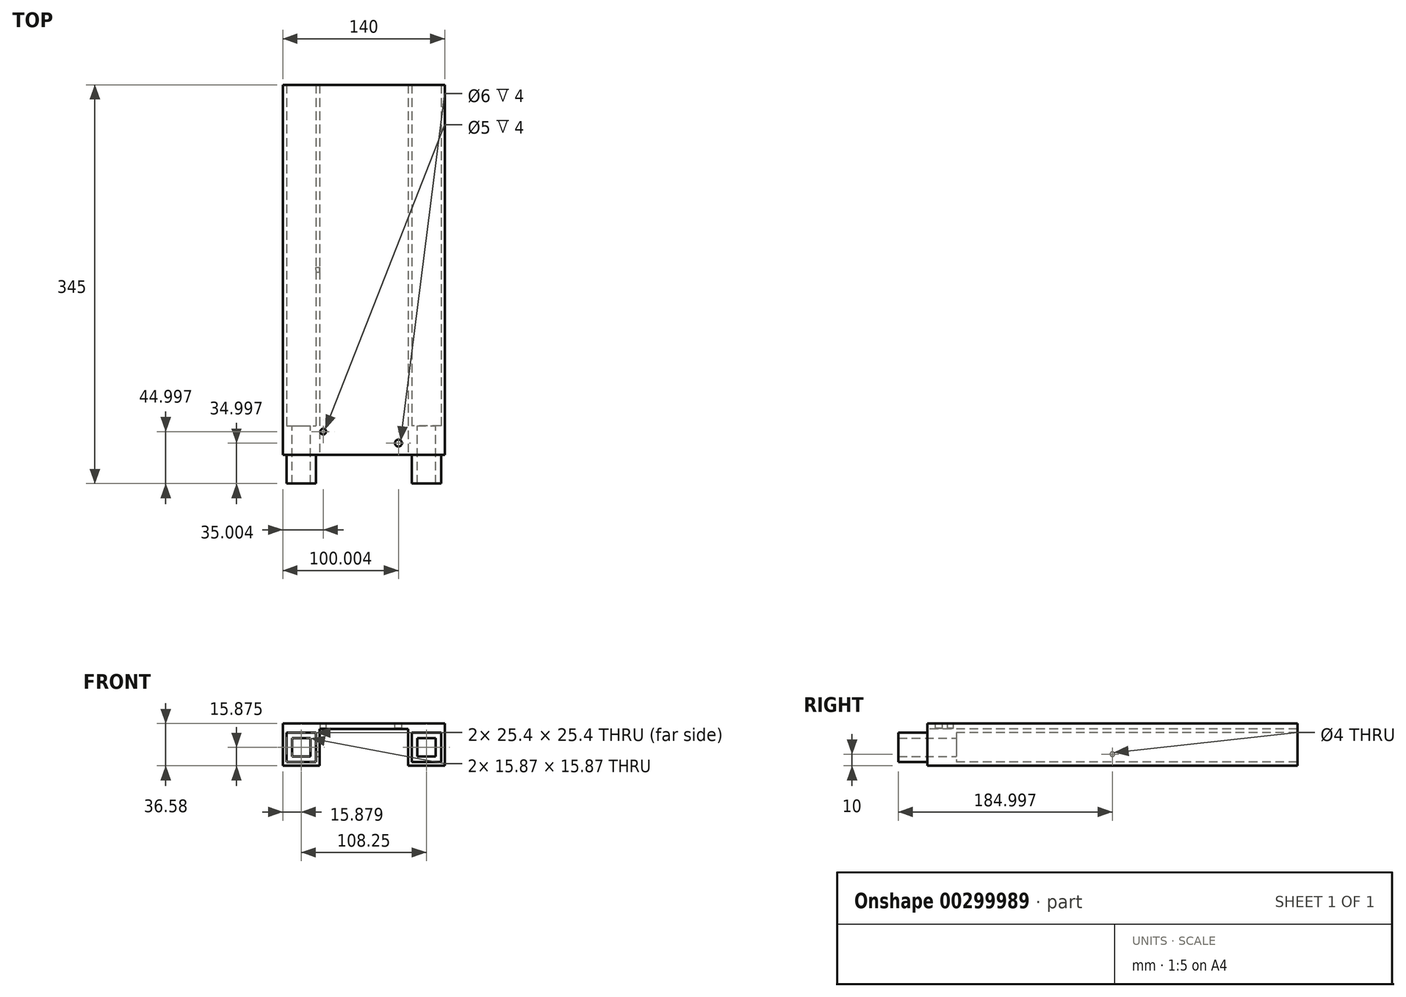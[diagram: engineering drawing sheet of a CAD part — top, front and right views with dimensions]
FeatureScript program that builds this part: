
annotation { "Feature Type Name" : "Feature", "Feature Type Description" : "" }
export const myFeature = defineFeature(function(context is Context, id is Id, definition is map)
    precondition{}
    {
        {
            var Q0;
            Q0=qCreatedBy(makeId("Top.planeOp"),FACE);
            var sketch = newSketch(context, id + "F0", { "sketchPlane" : qUnion([Q0])});
            skLineSegment(sketch, "E0.bottom", {"start": v(-71.28, 277.03) * mm, "end": v(68.72, 277.03) * mm});
            skLineSegment(sketch, "E0.top", {"start": v(-71.28, -42.97) * mm, "end": v(68.72, -42.97) * mm});
            skLineSegment(sketch, "E0.left", {"start": v(-71.28, 277.03) * mm, "end": v(-71.28, -42.97) * mm});
            skLineSegment(sketch, "E0.right", {"start": v(68.72, 277.03) * mm, "end": v(68.72, -42.97) * mm});
            skSolve(sketch);
        }
        {
            var Q0;
            Q0=makeQuery(id+"F0.imprint","IMPRINT",FACE,{"disambiguationData":[TD([[makeQuery(id+"F0.imprint","IMPRINT",EDGE,{"derivedFrom":sQuery(id+"F0.wireOp",EDGE,"E0.bottom")}),-1.0]])]});
            extrude(context, id + "F1", {"entities" : qUnion([Q0]), "depth" : 4.83 * mm, "offsetDistance" : 25 * mm});
        }
        {
            var Q0;
            Q0=makeQuery(id+"F1.opExtrude","SWEPT_FACE",FACE,{"disambiguationData":[OSD([sQuery(id+"F0.wireOp",EDGE,"E0.top")])]});
            var sketch = newSketch(context, id + "F2", { "sketchPlane" : qUnion([Q0])});
            skLineSegment(sketch, "E1.bottom", {"start": v(-71.28, 0) * mm, "end": v(-39.53, 0) * mm});
            skLineSegment(sketch, "E1.top", {"start": v(-71.28, -31.75) * mm, "end": v(-39.53, -31.75) * mm});
            skLineSegment(sketch, "E1.left", {"start": v(-71.28, 0) * mm, "end": v(-71.28, -31.75) * mm});
            skLineSegment(sketch, "E1.right", {"start": v(-39.53, 0) * mm, "end": v(-39.53, -31.75) * mm});
            skLineSegment(sketch, "E2.bottom", {"start": v(-68.1, -3.17) * mm, "end": v(-42.7, -3.17) * mm});
            skLineSegment(sketch, "E2.top", {"start": v(-68.1, -28.57) * mm, "end": v(-42.7, -28.57) * mm});
            skLineSegment(sketch, "E2.left", {"start": v(-68.1, -3.17) * mm, "end": v(-68.1, -28.57) * mm});
            skLineSegment(sketch, "E2.right", {"start": v(-42.7, -3.17) * mm, "end": v(-42.7, -28.57) * mm});
            skLineSegment(sketch, "E3.bottom", {"start": v(68.72, 0) * mm, "end": v(36.97, 0) * mm});
            skLineSegment(sketch, "E3.top", {"start": v(68.72, -31.75) * mm, "end": v(36.97, -31.75) * mm});
            skLineSegment(sketch, "E3.left", {"start": v(68.72, 0) * mm, "end": v(68.72, -31.75) * mm});
            skLineSegment(sketch, "E3.right", {"start": v(36.97, 0) * mm, "end": v(36.97, -31.75) * mm});
            skLineSegment(sketch, "E4.bottom", {"start": v(65.55, -3.17) * mm, "end": v(40.15, -3.18) * mm});
            skLineSegment(sketch, "E4.top", {"start": v(65.55, -28.57) * mm, "end": v(40.15, -28.57) * mm});
            skLineSegment(sketch, "E4.left", {"start": v(65.55, -3.17) * mm, "end": v(65.55, -28.57) * mm});
            skLineSegment(sketch, "E4.right", {"start": v(40.15, -3.18) * mm, "end": v(40.15, -28.57) * mm});
            skSolve(sketch);
        }
        {
            var Q0;
            Q0 = qSketchRegion(id + "F2", true);
            extrude(context, id + "F3", {"entities" : qUnion([Q0]), "operationType" : NewBodyOperationType.ADD, "oppositeDirection" : true, "depth" : 320 * mm});
        }
        {
            var Q0;
            Q0=makeQuery(id+"F3.boolean.opBoolean","MERGE",FACE,{"derivedFrom":[makeQuery(id+"F1.opExtrude","SWEPT_FACE",FACE,{"disambiguationData":[OSD([sQuery(id+"F0.wireOp",EDGE,"E0.top")])]}),makeQuery(id+"F3.opExtrude","CAP_FACE",FACE,{"disambiguationData":[OSD([sQuery(id+"F2.wireOp",EDGE,"E1.bottom"),sQuery(id+"F2.wireOp",EDGE,"E1.top"),sQuery(id+"F2.wireOp",EDGE,"E1.left"),sQuery(id+"F2.wireOp",EDGE,"E1.right"),sQuery(id+"F2.wireOp",EDGE,"E2.bottom"),sQuery(id+"F2.wireOp",EDGE,"E2.top"),sQuery(id+"F2.wireOp",EDGE,"E2.left"),sQuery(id+"F2.wireOp",EDGE,"E2.right")])],"isStart":true}),makeQuery(id+"F3.opExtrude","CAP_FACE",FACE,{"disambiguationData":[OSD([sQuery(id+"F2.wireOp",EDGE,"E3.bottom"),sQuery(id+"F2.wireOp",EDGE,"E3.top"),sQuery(id+"F2.wireOp",EDGE,"E3.left"),sQuery(id+"F2.wireOp",EDGE,"E3.right"),sQuery(id+"F2.wireOp",EDGE,"E4.bottom"),sQuery(id+"F2.wireOp",EDGE,"E4.top"),sQuery(id+"F2.wireOp",EDGE,"E4.left"),sQuery(id+"F2.wireOp",EDGE,"E4.right")])],"isStart":true})]});
            var sketch = newSketch(context, id + "F4", { "sketchPlane" : qUnion([Q0])});
            skLineSegment(sketch, "E5.bottom", {"start": v(-68.1, -3.17) * mm, "end": v(-42.7, -3.17) * mm});
            skLineSegment(sketch, "E5.top", {"start": v(-68.1, -28.57) * mm, "end": v(-42.7, -28.57) * mm});
            skLineSegment(sketch, "E5.left", {"start": v(-68.1, -3.17) * mm, "end": v(-68.1, -28.57) * mm});
            skLineSegment(sketch, "E5.right", {"start": v(-42.7, -3.17) * mm, "end": v(-42.7, -28.57) * mm});
            skLineSegment(sketch, "E6.bottom", {"start": v(40.15, -3.18) * mm, "end": v(65.55, -3.18) * mm});
            skLineSegment(sketch, "E6.top", {"start": v(40.15, -28.57) * mm, "end": v(65.55, -28.57) * mm});
            skLineSegment(sketch, "E6.left", {"start": v(40.15, -3.18) * mm, "end": v(40.15, -28.57) * mm});
            skLineSegment(sketch, "E6.right", {"start": v(65.55, -3.18) * mm, "end": v(65.55, -28.57) * mm});
            skLineSegment(sketch, "E7.bottom", {"start": v(-63.34, -7.94) * mm, "end": v(-47.46, -7.94) * mm});
            skLineSegment(sketch, "E7.top", {"start": v(-63.34, -23.81) * mm, "end": v(-47.46, -23.81) * mm});
            skLineSegment(sketch, "E7.left", {"start": v(-63.34, -7.94) * mm, "end": v(-63.34, -23.81) * mm});
            skLineSegment(sketch, "E7.right", {"start": v(-47.46, -7.94) * mm, "end": v(-47.46, -23.81) * mm});
            skLineSegment(sketch, "E8.bottom", {"start": v(44.91, -7.94) * mm, "end": v(60.79, -7.94) * mm});
            skLineSegment(sketch, "E8.top", {"start": v(44.91, -23.81) * mm, "end": v(60.79, -23.81) * mm});
            skLineSegment(sketch, "E8.left", {"start": v(44.91, -7.94) * mm, "end": v(44.91, -23.81) * mm});
            skLineSegment(sketch, "E8.right", {"start": v(60.79, -7.94) * mm, "end": v(60.79, -23.81) * mm});
            skSolve(sketch);
        }
        {
            var Q0;
            Q0 = qSketchRegion(id + "F4", true);
            extrude(context, id + "F5", {"entities" : qUnion([Q0]), "operationType" : NewBodyOperationType.ADD, "endBound" : BoundingType.SYMMETRIC, "depth" : 50 * mm, "offsetDistance" : 25 * mm});
        }
        {
            var Q0;
            Q0=makeQuery(id+"F3.opExtrude","SWEPT_FACE",FACE,{"disambiguationData":[OSD([sQuery(id+"F2.wireOp",EDGE,"E1.right")])]});
            var sketch = newSketch(context, id + "F6", { "sketchPlane" : qUnion([Q0])});
            skCircle(sketch, "E9", {"center": v(117.03, -21.75) * mm, "radius": 2 * mm});
            skSolve(sketch);
        }
        {
            var Q0;
            Q0 = qSketchRegion(id + "F6", true);
            extrude(context, id + "F7", {"entities" : qUnion([Q0]), "operationType" : NewBodyOperationType.REMOVE, "oppositeDirection" : true, "depth" : 4 * mm});
        }
        {
            var Q0;
            Q0=makeQuery(id+"F1.opExtrude","CAP_FACE",FACE,{"disambiguationData":[OSD([sQuery(id+"F0.wireOp",EDGE,"E0.bottom"),sQuery(id+"F0.wireOp",EDGE,"E0.top"),sQuery(id+"F0.wireOp",EDGE,"E0.left"),sQuery(id+"F0.wireOp",EDGE,"E0.right")])],"isStart":false});
            var sketch = newSketch(context, id + "F8", { "sketchPlane" : qUnion([Q0])});
            skCircle(sketch, "E10", {"center": v(-36.28, -22.97) * mm, "radius": 2.5 * mm});
            skCircle(sketch, "E11", {"center": v(28.72, -32.97) * mm, "radius": 3 * mm});
            skSolve(sketch);
        }
        {
            var Q0;
            Q0 = qSketchRegion(id + "F8", true);
            extrude(context, id + "F9", {"entities" : qUnion([Q0]), "operationType" : NewBodyOperationType.REMOVE, "oppositeDirection" : true, "depth" : 4 * mm});
        }
    });
